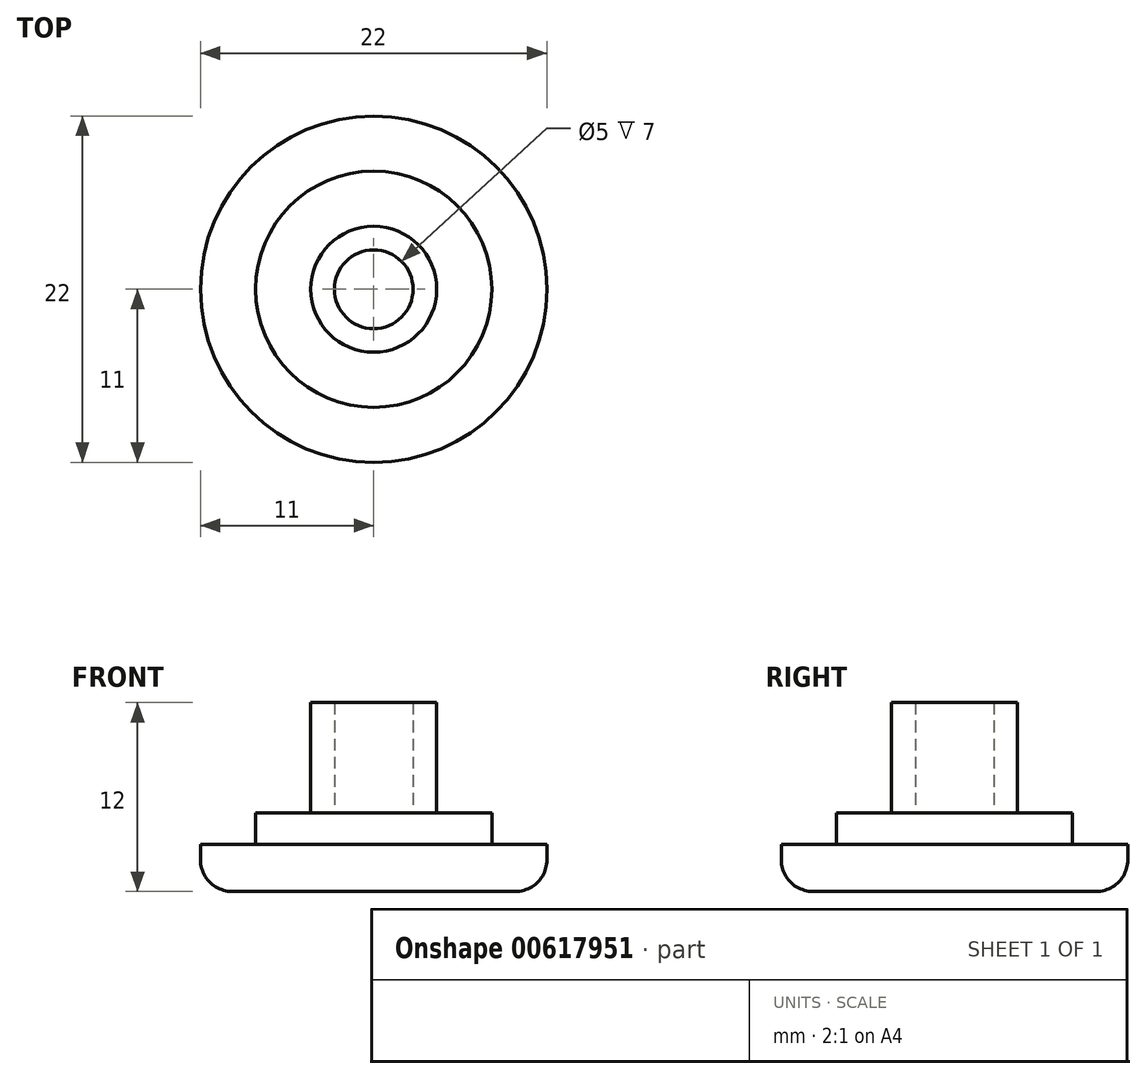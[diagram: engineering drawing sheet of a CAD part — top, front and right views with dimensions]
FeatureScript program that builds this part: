
annotation { "Feature Type Name" : "Feature", "Feature Type Description" : "" }
export const myFeature = defineFeature(function(context is Context, id is Id, definition is map)
    precondition{}
    {
        {
            var Q0;
            Q0=qCreatedBy(makeId("Top.planeOp"),FACE);
            var sketch = newSketch(context, id + "F0", { "sketchPlane" : qUnion([Q0])});
            skCircle(sketch, "E0", {"center": v(0, 0) * mm, "radius": 11 * mm});
            skSolve(sketch);
        }
        {
            var Q0;
            Q0=makeQuery(id+"F0.imprint","IMPRINT",FACE,{"disambiguationData":[TD([[makeQuery(id+"F0.imprint","IMPRINT",EDGE,{"derivedFrom":sQuery(id+"F0.wireOp",EDGE,"E0")}),1.0]])]});
            extrude(context, id + "F1", {"entities" : qUnion([Q0]), "depth" : 3 * mm, "offsetDistance" : 25 * mm});
        }
        {
            var Q0;
            Q0=makeQuery(id+"F1.opExtrude","CAP_EDGE",EDGE,{"disambiguationData":[OSD([sQuery(id+"F0.wireOp",EDGE,"E0")])],"isStart":true});
            fillet(context, id + "F2", {"entities" : qUnion([Q0]), "radius" : 2 * mm, "tangentPropagation" : true, "allowEdgeOverflow" : false});
        }
        {
            var Q0;
            Q0=makeQuery(id+"F1.opExtrude","CAP_FACE",FACE,{"disambiguationData":[OSD([sQuery(id+"F0.wireOp",EDGE,"E0")])],"isStart":false});
            var sketch = newSketch(context, id + "F3", { "sketchPlane" : qUnion([Q0])});
            skCircle(sketch, "E1", {"center": v(0, 0) * mm, "radius": 7.5 * mm});
            skSolve(sketch);
        }
        {
            var Q0;
            Q0=makeQuery(id+"F3.imprint","IMPRINT",FACE,{"disambiguationData":[TD([[makeQuery(id+"F3.imprint","IMPRINT",EDGE,{"derivedFrom":sQuery(id+"F3.wireOp",EDGE,"E1")}),1.0]])]});
            extrude(context, id + "F4", {"entities" : qUnion([Q0]), "operationType" : NewBodyOperationType.ADD, "depth" : 2 * mm, "offsetDistance" : 25 * mm});
        }
        {
            var Q0;
            Q0=makeQuery(id+"F4.opExtrude","CAP_FACE",FACE,{"disambiguationData":[OSD([sQuery(id+"F3.wireOp",EDGE,"E1")])],"isStart":false});
            var sketch = newSketch(context, id + "F5", { "sketchPlane" : qUnion([Q0])});
            skCircle(sketch, "E2", {"center": v(0, 0) * mm, "radius": 4 * mm});
            skCircle(sketch, "E3", {"center": v(0, 0) * mm, "radius": 2.5 * mm});
            skSolve(sketch);
        }
        {
            var Q0;
            Q0 = qSketchRegion(id + "F5", true);
            extrude(context, id + "F6", {"entities" : qUnion([Q0]), "operationType" : NewBodyOperationType.ADD, "depth" : 7 * mm, "offsetDistance" : 25 * mm});
        }
    });
